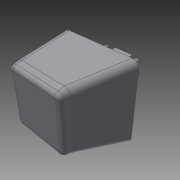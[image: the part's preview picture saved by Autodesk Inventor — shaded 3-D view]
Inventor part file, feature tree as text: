
AUTODESK INVENTOR PART (.ipt)
format: ipt  version: 2014 (Build 180170000, 170)  size: 521,728 bytes
history: native  units: mm
features: extrude x13, sketch x13, chamfer x11, fillet x6
ambient origin geometry x8: Origin, YZ Plane, XZ Plane, XY Plane, X Axis, Y Axis, Z Axis, Center Point
bodies: Solid1 (feature_tree)
feature tree (43):
  extrude  "Extrusion1"  Depth=18.0mm
  extrude  "Extrusion2"  Depth=1.0mm
  chamfer  "Chamfer1"  Distance=10.0mm
  chamfer  "Chamfer2"  Distance=4.0mm Angle=45.0deg
  chamfer  "Chamfer3"  Distance=11.0mm Angle=45.0deg
  chamfer  "Chamfer4"  Distance=10.0mm Angle=45.0deg
  chamfer  "Chamfer5"  Distance=11.0mm Angle=45.0deg
  chamfer  "Chamfer6"  Distance=10.0mm Angle=45.0deg
  fillet  "Fillet4"  Radius=1.5mm
  fillet  "Fillet7"  Radius=1.0mm
  extrude  "Extrusion4"  Depth=1.0mm TaperAngle=0.0deg
  extrude  "Extrusion5"  Depth=1.0mm TaperAngle=0.0deg
  extrude  "Extrusion6"  Depth=1.0mm TaperAngle=0.0deg
  extrude  "Extrusion7"  Depth=1.5mm TaperAngle=0.0deg
  extrude  "Extrusion8"  Depth=1.0mm TaperAngle=0.0deg
  extrude  "Extrusion9"  Depth=1.5mm TaperAngle=0.0deg
  extrude  "Extrusion10"  Depth=1.5mm TaperAngle=45.0deg
  extrude  "Extrusion11"  Depth=1.0mm TaperAngle=45.0deg
  extrude  "Extrusion12"  Depth=1.0mm
  chamfer  "Chamfer7"  Distance=1.4mm Angle=45.0deg
  chamfer  "Chamfer8"  Distance=0.15mm Angle=45.0deg
  fillet  "Fillet8"  Radius=0.1mm
  chamfer  "Chamfer9"  Distance=2.0mm
  chamfer  "Chamfer10"  Distance=0.5mm Angle=45.0deg
  fillet  "Fillet9"  Radius=1.0mm
  extrude  "Extrusion13"  Depth=1.0mm
  chamfer  "Chamfer11"  Distance=1.0mm
  extrude  "Extrusion14"  [1 undecoded]
  fillet  "Fillet10"  [1 undecoded]
  fillet  "Fillet11"  [1 undecoded]
  sketch  "Sketch1"  dims[d2=18.0mm d3=18.0mm]
  sketch  "Sketch2"  dims[d4=1.0mm d5=0.0mm d6=5.0mm]
  sketch  "Sketch6"  dims[d7=5.0mm]
  sketch  "Sketch7"  dims[d8=3.0mm]
  sketch  "Sketch8"  dims[d9=3.0mm]
  sketch  "Sketch9"  dims[d10=3.0mm]
  sketch  "Sketch10"  dims[d11=3.0mm]
  sketch  "Sketch12"  dims[d12=1.0mm]
  sketch  "Sketch13"  dims[d13=1.0mm d14=10.0mm d15=0.0mm d16=4.0mm d17=10.0mm d18=45.0deg d19=11.0mm d20=4.0mm d21=45.0deg d22=10.0mm d23=2.0mm d24=45.0deg d25=11.0mm d26=2.0mm d27=45.0deg d28=10.0mm d29=2.0mm d30=45.0deg]
  sketch  "Sketch14"  dims[d31=11.0mm d32=2.0mm d33=45.0deg d39=1.5mm d42=1.0mm]
  sketch  "Sketch15"  dims[d43=1.0mm d44=0.0mm d62=18.0mm d63=0.0mm]
  sketch  "Sketch16"  dims[d64=10.0mm d65=0.0mm d66=1.0mm d67=0.0mm]
  sketch  "Sketch17"  dims[d68=1.0mm d69=0.0mm d70=2.0mm d71=0.0mm d72=1.5mm d73=0.0mm d74=2.0mm d75=0.0mm d76=1.5mm d77=0.0mm d78=1.5mm d79=0.25mm d80=45.0deg d81=0.15mm d82=0.2mm d83=45.0deg d84=0.1mm d85=1.4mm d86=0.2mm d87=45.0deg d88=0.15mm d89=0.45mm d90=45.0deg d91=0.1mm d92=2.0mm d93=0.0mm d94=0.5mm d95=2.0mm d96=45.0deg d97=1.0mm d98=0.0mm d99=1.0mm d100=1.0mm]
note: 3 required parameter values undecoded (feature->parameter linkage not recoverable at this tier; creation-order binding heuristic only, values carry confidence <= 0.55)
